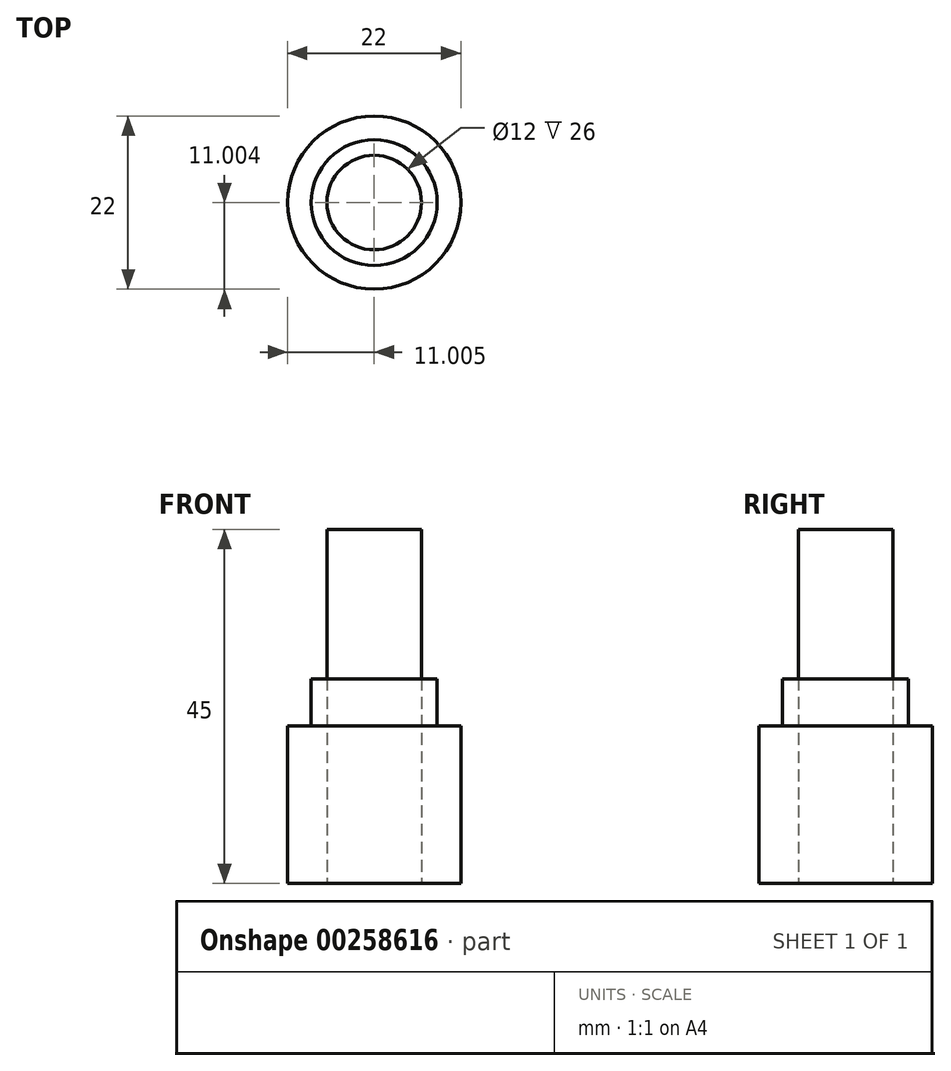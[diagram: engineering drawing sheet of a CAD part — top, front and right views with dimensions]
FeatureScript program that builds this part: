
annotation { "Feature Type Name" : "Feature", "Feature Type Description" : "" }
export const myFeature = defineFeature(function(context is Context, id is Id, definition is map)
    precondition{}
    {
        {
            var Q0;
            Q0=qCreatedBy(makeId("Top.planeOp"),FACE);
            var sketch = newSketch(context, id + "F0", { "sketchPlane" : qUnion([Q0])});
            skPoint(sketch, "E0", {"position": v(-35.28, -8) * mm});
            skCircle(sketch, "E1", {"center": v(-35.28, -8) * mm, "radius": 11 * mm});
            skCircle(sketch, "E2", {"center": v(-35.28, -8) * mm, "radius": 8 * mm});
            skCircle(sketch, "E3", {"center": v(-35.28, -8) * mm, "radius": 6 * mm});
            skSolve(sketch);
        }
        {
            var Q0;
            Q0=makeQuery(id+"F0.imprint","IMPRINT",FACE,{"disambiguationData":[TD([[makeQuery(id+"F0.imprint","IMPRINT",EDGE,{"derivedFrom":sQuery(id+"F0.wireOp",EDGE,"E3")}),1.0]])]});
            var Q1;
            Q1=sQuery(id+"F0.wireOp",EDGE,"E3");
            extrude(context, id + "F1", {"entities" : qUnion([Q0]), "surfaceEntities" : qUnion([Q1]), "depth" : 45 * mm});
        }
        {
            var Q0;
            Q0=makeQuery(id+"F0.imprint","IMPRINT",FACE,{"disambiguationData":[TD([[makeQuery(id+"F0.imprint","IMPRINT",EDGE,{"derivedFrom":sQuery(id+"F0.wireOp",EDGE,"E2")}),1.0]])]});
            var Q1;
            Q1=sQuery(id+"F0.wireOp",EDGE,"E2");
            extrude(context, id + "F2", {"entities" : qUnion([Q0]), "surfaceEntities" : qUnion([Q1]), "depth" : 26 * mm});
        }
        {
            var Q0;
            Q0=makeQuery(id+"F0.imprint","IMPRINT",FACE,{"disambiguationData":[TD([[makeQuery(id+"F0.imprint","IMPRINT",EDGE,{"derivedFrom":sQuery(id+"F0.wireOp",EDGE,"E1")}),1.0]])]});
            var Q1;
            Q1=sQuery(id+"F0.wireOp",EDGE,"E1");
            extrude(context, id + "F3", {"entities" : qUnion([Q0]), "operationType" : NewBodyOperationType.ADD, "surfaceEntities" : qUnion([Q1]), "depth" : 20 * mm});
        }
    });
